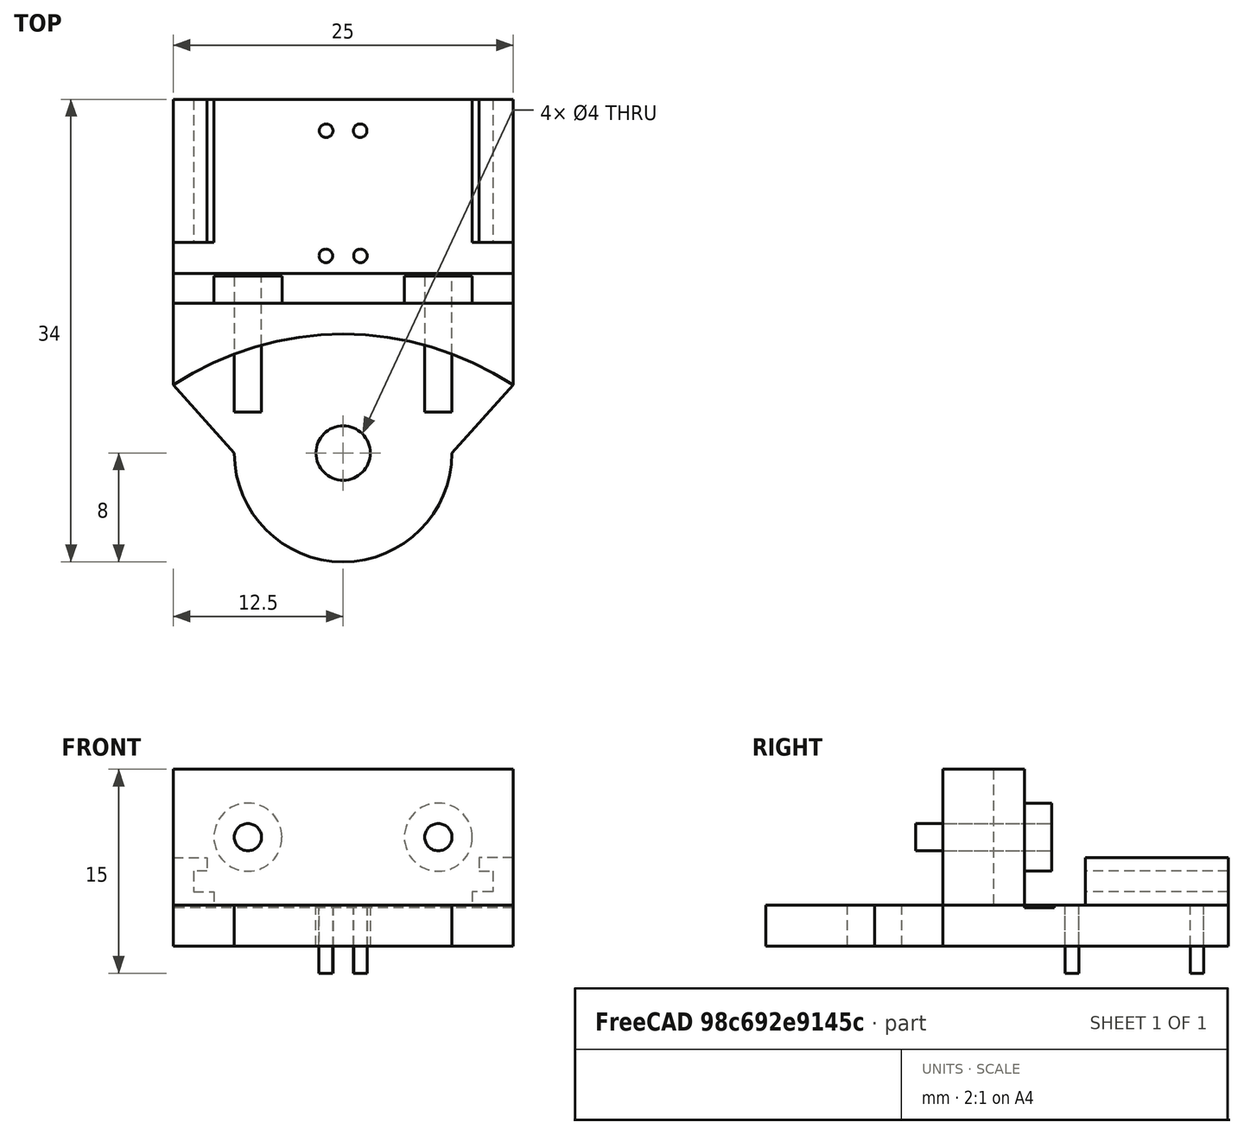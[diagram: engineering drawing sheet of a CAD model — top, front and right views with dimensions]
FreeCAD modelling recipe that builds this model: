
FCSTD DOCUMENT  (FreeCAD 0.16R4740 (Git))
Label: base
License: All rights reserved
LicenseURL: http://en.wikipedia.org/wiki/All_rights_reserved
objects: Sketcher::SketchObject×7, PartDesign::Pad×4, PartDesign::Pocket×3, Mesh::Feature×1
note: 21 computed .brp shape members not serialized (recipe doc carries the construction recipe); baked Part::Feature solids carry a one-line shape summary decoded from their .brp

FEATURE [Sketcher::SketchObject] Sketch
  sketch-geometry (7):
    g0: Circle CenterX=0 CenterY=-11 CenterZ=0 NormalX=0 NormalY=0 NormalZ=1 Radius=2
    g1: LineSegment StartX=-12.5 StartY=15 StartZ=0 EndX=12.5 EndY=15 EndZ=0
    g2: LineSegment StartX=12.5 StartY=15 StartZ=0 EndX=12.5 EndY=-6 EndZ=0
    g3: LineSegment StartX=-12.5 StartY=15 StartZ=0 EndX=-12.5 EndY=-6 EndZ=0
    g4: LineSegment StartX=-12.5 StartY=-6 StartZ=0 EndX=-8 EndY=-11 EndZ=0
    g5: LineSegment StartX=12.5 StartY=-6 StartZ=0 EndX=8 EndY=-11 EndZ=0
    g6: ArcOfCircle CenterX=0 CenterY=-11 CenterZ=0 NormalX=0 NormalY=0 NormalZ=1 Radius=8 StartAngle=3.14159 EndAngle=6.28319
  constraints (20):
    c: Radius(g0) = 2
    c: Horizontal(g1)
    c: Coincident(g2,g1)
    c: Vertical(g2)
    c: Coincident(g3,g1)
    c: Vertical(g3)
    c: PointOnObject(g0,g-2)
    c: DistanceY(g-1,g0) = -11
    c: Coincident(g4,g3)
    c: Coincident(g5,g2)
    c: Symmetric(g4,g5,g-2)
    c: Coincident(g6,g0)
    c: Coincident(g6,g4)
    c: Coincident(g6,g5)
    c: DistanceY(g4,g0) = 0
    c: Symmetric(g3,g2,g-2)
    c: DistanceY(g-1,g3) = -6
    c: DistanceX(g1) = 25
    c: DistanceY(g-1,g1) = 15
    c: Distance(g0,g4) = 8
FEATURE [PartDesign::Pad] Pad
  Length = 3
  Length2 = 100
  Reversed = true
  Sketch = -> Sketch
  Type = 0
FEATURE [Sketcher::SketchObject] Sketch001
  ExternalGeometry = -> [Pad]
  Support = -> Pad [Face8]
  sketch-geometry (4):
    g0: LineSegment StartX=-12.5 StartY=0 StartZ=0 EndX=-12.5 EndY=-6 EndZ=0
    g1: LineSegment StartX=-12.5 StartY=0 StartZ=0 EndX=12.5 EndY=0 EndZ=0
    g2: LineSegment StartX=12.5 StartY=0 StartZ=0 EndX=12.5 EndY=-6 EndZ=0
    g3: ArcOfCircle CenterX=0 CenterY=-25 CenterZ=0 NormalX=0 NormalY=0 NormalZ=1 Radius=22.7431 StartAngle=0.988891 EndAngle=2.1527
  constraints (12):
    c: Coincident(g1,g0)
    c: PointOnObject(g1,g-1)
    c: Horizontal(g1)
    c: Coincident(g2,g1)
    c: Vertical(g2)
    c: Coincident(g3,g0)
    c: Coincident(g3,g2)
    c: Parallel(g0,g2)
    c: PointOnObject(g3,g-2)
    c: Distance(g1) = 25
    c: Coincident(g0,g-3)
    c: DistanceY(g-1,g3) = -25
FEATURE [PartDesign::Pad] Pad001
  Length = 10
  Length2 = 100
  Sketch = -> Sketch001
  Type = 0
FEATURE [Sketcher::SketchObject] Sketch002
  Placement = pos=(12.5,0,0) rot=(0.57735,0.57735,0.57735;2.0944rad)
  Support = -> Pad001 [Face3]
  sketch-geometry (4):
    g0: LineSegment StartX=0 StartY=0 StartZ=0 EndX=2.2 EndY=0 EndZ=0
    g1: LineSegment StartX=2.2 StartY=0 StartZ=0 EndX=2.2 EndY=-0.2 EndZ=0
    g2: LineSegment StartX=2.2 StartY=-0.2 StartZ=0 EndX=0 EndY=-0.2 EndZ=0
    g3: LineSegment StartX=0 StartY=-0.2 StartZ=0 EndX=0 EndY=0 EndZ=0
  constraints (11):
    c: Coincident(g0,g1)
    c: Coincident(g1,g2)
    c: Coincident(g2,g3)
    c: Coincident(g3,g0)
    c: Horizontal(g0)
    c: Horizontal(g2)
    c: Vertical(g1)
    c: Vertical(g3)
    c: Coincident(g0,g-1)
    c: Distance(g2) = 2.2
    c: Distance(g1) = 0.2
FEATURE [PartDesign::Pocket] Pocket
  Length = 25
  Sketch = -> Sketch002
  Type = 0
FEATURE [Sketcher::SketchObject] Sketch004
  ExternalGeometry = -> [Pocket]
  Placement = pos=(0,15,0) rot=(0,0.707107,0.707107;3.14159rad)
  Support = -> Pocket [Face1]
  sketch-geometry (16):
    g0: LineSegment StartX=12.5 StartY=0 StartZ=0 EndX=12.5 EndY=3.5 EndZ=0
    g1: LineSegment StartX=12.5 StartY=3.5 StartZ=0 EndX=10 EndY=3.5 EndZ=0
    g2: LineSegment StartX=10 StartY=2.5 StartZ=0 EndX=11 EndY=2.5 EndZ=0
    g3: LineSegment StartX=11 StartY=2.5 StartZ=0 EndX=11 EndY=1 EndZ=0
    g4: LineSegment StartX=11 StartY=1 StartZ=0 EndX=9.5 EndY=1 EndZ=0
    g5: LineSegment StartX=9.5 StartY=1 StartZ=0 EndX=9.5 EndY=0 EndZ=0
    g6: LineSegment StartX=9.5 StartY=0 StartZ=0 EndX=12.5 EndY=0 EndZ=0
    g7: LineSegment StartX=10 StartY=3.5 StartZ=0 EndX=10 EndY=2.5 EndZ=0
    g8: LineSegment StartX=-12.5 StartY=0 StartZ=0 EndX=-12.5 EndY=3.5 EndZ=0
    g9: LineSegment StartX=-12.5 StartY=3.5 StartZ=0 EndX=-10 EndY=3.5 EndZ=0
    g10: LineSegment StartX=-10 StartY=3.5 StartZ=0 EndX=-10 EndY=2.5 EndZ=0
    g11: LineSegment StartX=-10 StartY=2.5 StartZ=0 EndX=-11 EndY=2.5 EndZ=0
    g12: LineSegment StartX=-11 StartY=2.5 StartZ=0 EndX=-11 EndY=1 EndZ=0
    g13: LineSegment StartX=-11 StartY=1 StartZ=0 EndX=-9.5 EndY=1 EndZ=0
    g14: LineSegment StartX=-9.5 StartY=1 StartZ=0 EndX=-9.5 EndY=0 EndZ=0
    g15: LineSegment StartX=-9.5 StartY=0 StartZ=0 EndX=-12.5 EndY=0 EndZ=0
  constraints (46):
    c: Coincident(g0,g1)
    c: Coincident(g2,g3)
    c: Coincident(g3,g4)
    c: Coincident(g4,g5)
    c: Coincident(g5,g6)
    c: Coincident(g0,g6)
    c: Coincident(g1,g7)
    c: Coincident(g2,g7)
    c: Vertical(g0)
    c: Vertical(g3)
    c: Vertical(g7)
    c: Vertical(g5)
    c: Horizontal(g1)
    c: Horizontal(g2)
    c: Horizontal(g4)
    c: Horizontal(g6)
    c: Distance(g1) = 2.5
    c: Distance(g3) = 1.5
    c: Distance(g5) = 1
    c: Distance(g0) = 3.5
    c: Coincident(g0,g-3)
    c: Vertical(g8)
    c: Horizontal(g9)
    c: Coincident(g10,g9)
    c: Coincident(g11,g10)
    c: Horizontal(g11)
    c: Coincident(g12,g11)
    c: Vertical(g12)
    c: Coincident(g13,g12)
    c: Horizontal(g13)
    c: Coincident(g14,g13)
    c: Vertical(g14)
    c: Coincident(g15,g14)
    c: Horizontal(g15)
    c: Coincident(g8,g15)
    c: Coincident(g8,g-4)
    c: Vertical(g10)
    c: Distance(g9) = 2.5
    c: Coincident(g8,g9)
    c: Distance(g13) = 1.5
    c: Distance(g15) = 3
    c: Distance(g8) = 3.5
    c: Distance(g12) = 1.5
    c: Distance(g14) = 1
    c: Distance(g6) = 3
    c: Distance(g4) = 1.5
FEATURE [PartDesign::Pad] Pad002
  Length = 10.5
  Length2 = 100
  Reversed = true
  Sketch = -> Sketch004
  Type = 0
FEATURE [Sketcher::SketchObject] Sketch005
  Placement = pos=(0,0,0) rot=(0,0.707107,0.707107;3.14159rad)
  Support = -> Pad002 [Face34]
  sketch-geometry (2):
    g0: Circle CenterX=7 CenterY=5 CenterZ=0 NormalX=0 NormalY=0 NormalZ=1 Radius=2.5
    g1: Circle CenterX=-7 CenterY=5 CenterZ=0 NormalX=0 NormalY=0 NormalZ=1 Radius=2.5
  constraints (5):
    c: Radius(g0) = 2.5
    c: Radius(g1) = 2.5
    c: Symmetric(g1,g0,g-2)
    c: DistanceX(g-2,g0) = 7
    c: DistanceY(g-1,g1) = 5
FEATURE [PartDesign::Pad] Pad003
  Length = 2
  Length2 = 100
  Sketch = -> Sketch005
  Type = 0
FEATURE [Sketcher::SketchObject] Sketch006
  Placement = pos=(0,2,0) rot=(0,0.707107,0.707107;3.14159rad)
  Support = -> Pad003 [Face40]
  sketch-geometry (2):
    g0: Circle CenterX=-7 CenterY=5 CenterZ=0 NormalX=0 NormalY=0 NormalZ=1 Radius=1
    g1: Circle CenterX=7 CenterY=5 CenterZ=0 NormalX=0 NormalY=0 NormalZ=1 Radius=1
  constraints (5):
    c: Symmetric(g0,g1,g-2)
    c: Radius(g0) = 1
    c: Radius(g1) = 1
    c: DistanceX(g-1,g0) = -7
    c: DistanceY(g-1,g0) = 5
FEATURE [PartDesign::Pocket] Pocket001
  Length = 10
  Sketch = -> Sketch006
  Type = 0
FEATURE [Sketcher::SketchObject] Sketch007
  Support = -> Pocket001 [Face10]
  sketch-geometry (4):
    g0: Circle CenterX=-1.27 CenterY=3.5 CenterZ=0 NormalX=0 NormalY=0 NormalZ=1 Radius=0.5
    g1: Circle CenterX=1.27 CenterY=3.5 CenterZ=0 NormalX=0 NormalY=0 NormalZ=1 Radius=0.5
    g2: Circle CenterX=-1.25 CenterY=12.7 CenterZ=0 NormalX=0 NormalY=0 NormalZ=1 Radius=0.5
    g3: Circle CenterX=1.25 CenterY=12.7 CenterZ=0 NormalX=0 NormalY=0 NormalZ=1 Radius=0.5
  constraints (10):
    c: Radius(g0) = 0.5
    c: Radius(g1) = 0.5
    c: Radius(g2) = 0.5
    c: Radius(g3) = 0.5
    c: DistanceX(g2,g3) = 2.5
    c: DistanceX(g0,g1) = 2.54
    c: Symmetric(g2,g3,g-2)
    c: Symmetric(g0,g1,g-2)
    c: DistanceY(g2,g0) = -9.2
    c: DistanceY(g-1,g0) = 3.5
FEATURE [PartDesign::Pocket] Pocket002
  Length = 5
  Sketch = -> Sketch007
  Type = 0
FEATURE [Mesh::Feature] Mesh  label="Pocket002 (Meshed)"
